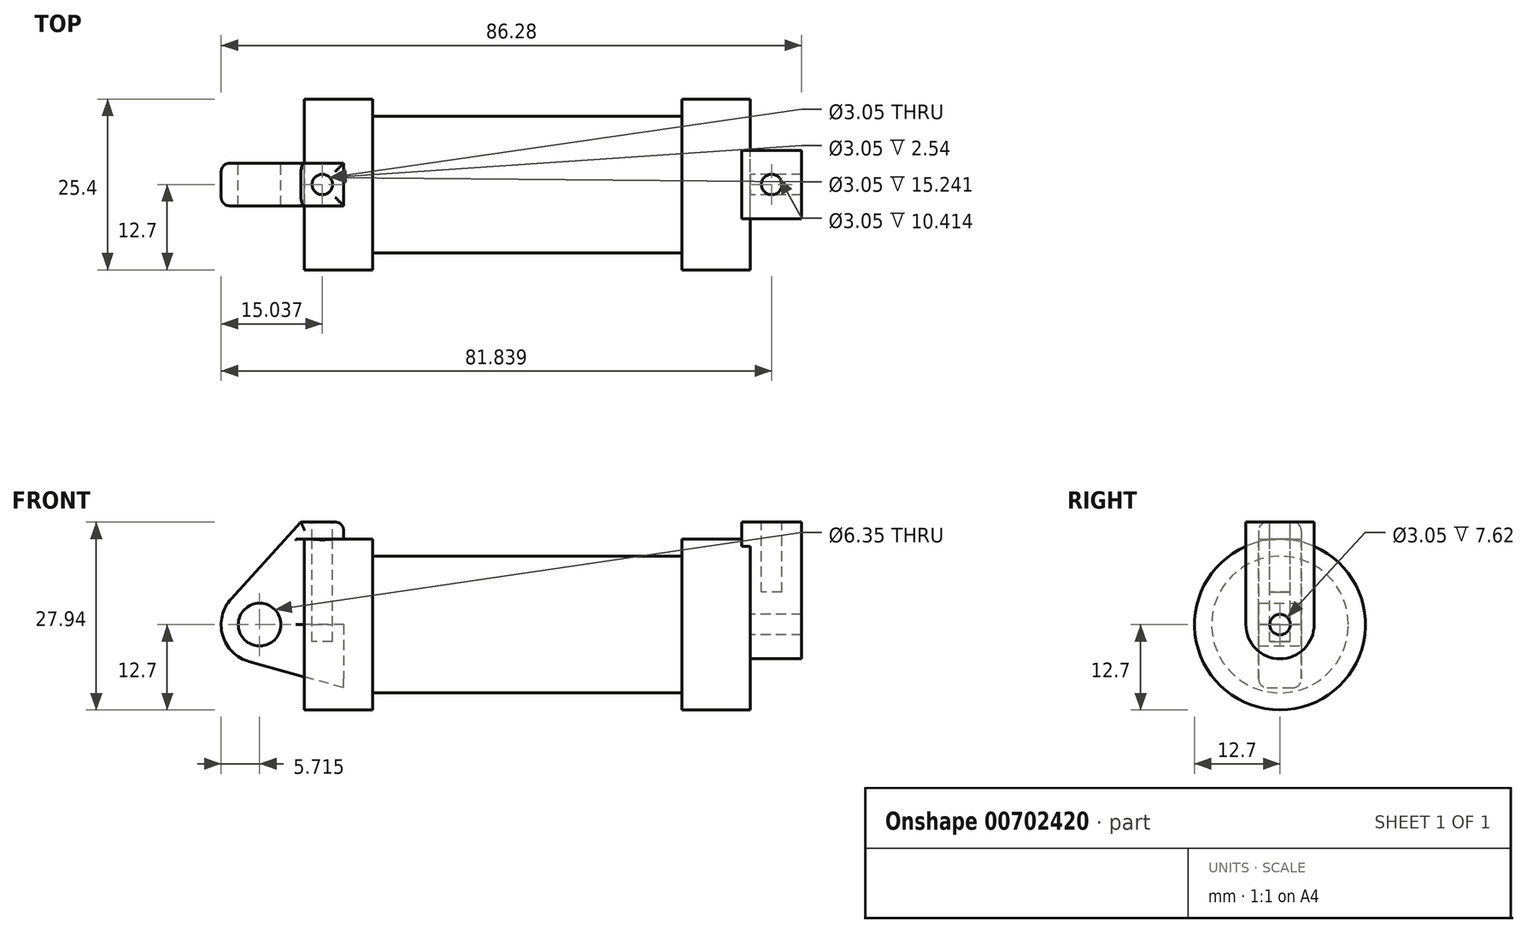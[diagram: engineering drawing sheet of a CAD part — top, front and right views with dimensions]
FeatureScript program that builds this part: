
annotation { "Feature Type Name" : "Feature", "Feature Type Description" : "" }
export const myFeature = defineFeature(function(context is Context, id is Id, definition is map)
    precondition{}
    {
        {
            var Q0;
            Q0=qCreatedBy(makeId("Front.planeOp"),FACE);
            var sketch = newSketch(context, id + "F0", { "sketchPlane" : qUnion([Q0])});
            skLineSegment(sketch, "E0", {"start": v(0, 0) * mm, "end": v(0, 12.7) * mm});
            skLineSegment(sketch, "E1", {"start": v(0, 12.7) * mm, "end": v(10.16, 12.7) * mm});
            skLineSegment(sketch, "E2", {"start": v(10.16, 12.7) * mm, "end": v(10.16, 10.16) * mm});
            skLineSegment(sketch, "E3", {"start": v(10.16, 10.16) * mm, "end": v(56.13, 10.16) * mm});
            skLineSegment(sketch, "E4", {"start": v(56.13, 10.16) * mm, "end": v(56.13, 12.7) * mm});
            skLineSegment(sketch, "E5", {"start": v(56.13, 12.7) * mm, "end": v(66.3, 12.7) * mm});
            skLineSegment(sketch, "E6", {"start": v(66.3, 12.7) * mm, "end": v(66.3, 0) * mm});
            skLineSegment(sketch, "E7", {"start": v(66.3, 0) * mm, "end": v(0, 0) * mm});
            skLineSegment(sketch, "E8", {"start": v(5.84, 15.24) * mm, "end": v(-0.5, 15.24) * mm});
            skLineSegment(sketch, "E9", {"start": v(-0.5, 15.24) * mm, "end": v(-10.88, 3.85) * mm});
            skLineSegment(sketch, "E10", {"start": v(0, 0) * mm, "end": v(-6.65, 0) * mm});
            skCircle(sketch, "E11", {"center": v(-6.65, 0) * mm, "radius": 5.72 * mm});
            skCircle(sketch, "E12", {"center": v(-6.65, 0) * mm, "radius": 3.18 * mm});
            skLineSegment(sketch, "E13", {"start": v(5.84, 15.24) * mm, "end": v(5.84, -9.4) * mm});
            skLineSegment(sketch, "E14", {"start": v(5.84, -9.4) * mm, "end": v(-8.18, -5.5) * mm});
            skSolve(sketch);
        }
        {
            var Q0;
            {var subQ0=sQuery(id+"F0.wireOp",EDGE,"E2");Q0=makeQuery(id+"F0.imprint","IMPRINT",FACE,{"disambiguationData":[TD([[makeQuery(id+"F0.imprint","IMPRINT",EDGE,{"derivedFrom":subQ0}),-1.0]])]});}
            var Q1;
            {var subQ0=sQuery(id+"F0.wireOp",EDGE,"E0");Q1=makeQuery(id+"F0.imprint","IMPRINT",FACE,{"disambiguationData":[TD([[makeQuery(id+"F0.imprint","IMPRINT",EDGE,{"derivedFrom":subQ0}),-1.0]])]});}
            var Q2;
            Q2=sQuery(id+"F0.wireOp",EDGE,"E3");
            var Q3;
            Q3=sQuery(id+"F0.wireOp",EDGE,"E7");
            revolve(context, id + "F1", {"entities" : qUnion([Q0, Q1]), "surfaceEntities" : qUnion([Q2]), "axis" : qUnion([Q3]), "revolveType" : RevolveType.FULL});
        }
        {
            var Q0;
            {var subQ1=sQuery(id+"F0.wireOp",EDGE,"E0");Q0=makeQuery(id+"F0.imprint","IMPRINT",FACE,{"disambiguationData":[TD([[makeQuery(id+"F0.imprint","IMPRINT",EDGE,{"derivedFrom":subQ1}),1.0]])]});}
            var Q1;
            {var subQ5=sQuery(id+"F0.wireOp",EDGE,"E12");Q1=makeQuery(id+"F0.imprint","IMPRINT",FACE,{"disambiguationData":[TD([[makeQuery(id+"F0.imprint","IMPRINT",EDGE,{"derivedFrom":subQ5}),-1.0]])]});}
            var Q2;
            {var subQ0=sQuery(id+"F0.wireOp",EDGE,"E14");Q2=makeQuery(id+"F0.imprint","IMPRINT",FACE,{"disambiguationData":[TD([[makeQuery(id+"F0.imprint","IMPRINT",EDGE,{"derivedFrom":subQ0}),-1.0]])]});}
            extrude(context, id + "F2", {"entities" : qUnion([Q0, Q1, Q2]), "endBound" : BoundingType.SYMMETRIC, "depth" : 6.35 * mm, "offsetDistance" : 25.4 * mm});
        }
        {
            var Q0;
            Q0=makeQuery(id+"F1.opRevolve","SWEPT_FACE",FACE,{"disambiguationData":[OSD([sQuery(id+"F0.wireOp",EDGE,"E6")])]});
            var sketch = newSketch(context, id + "F3", { "sketchPlane" : qUnion([Q0])});
            skCircle(sketch, "E15", {"center": v(0, 0) * mm, "radius": 1.52 * mm});
            skCircle(sketch, "E16", {"center": v(0, 0) * mm, "radius": 5.08 * mm});
            skLineSegment(sketch, "E17", {"start": v(5.08, 0) * mm, "end": v(5.08, 15.24) * mm});
            skLineSegment(sketch, "E18", {"start": v(-5.08, 0) * mm, "end": v(-5.08, 15.24) * mm});
            skLineSegment(sketch, "E19", {"start": v(-5.08, 15.24) * mm, "end": v(0, 15.24) * mm});
            skLineSegment(sketch, "E20", {"start": v(5.08, 15.24) * mm, "end": v(0, 15.24) * mm});
            skSolve(sketch);
        }
        {
            var Q0;
            {var subQ1=sQuery(id+"F3.wireOp",EDGE,"E19");Q0=makeQuery(id+"F3.imprint","IMPRINT",FACE,{"disambiguationData":[TD([[makeQuery(id+"F3.imprint","IMPRINT",EDGE,{"derivedFrom":subQ1}),-1.0]])]});}
            var Q1;
            {var subQ0=sQuery(id+"F3.wireOp",EDGE,"E17");var subQ1=sQuery(id+"F3.wireOp",EDGE,"E16");var subQ2=makeQuery(id+"F3.imprint","INTERSECT",VERTEX,{"derivedFrom":[subQ1,subQ0]});Q1=makeQuery(id+"F3.imprint","IMPRINT",FACE,{"disambiguationData":[TD([[makeQuery(id+"F3.imprint","IMPRINT",EDGE,{"disambiguationData":[TD([[subQ2,-1.0]])],"derivedFrom":subQ1}),-1.0]])]});}
            var Q2;
            Q2=makeQuery(id+"F3.imprint","IMPRINT",FACE,{"disambiguationData":[TD([[makeQuery(id+"F3.imprint","IMPRINT",EDGE,{"derivedFrom":sQuery(id+"F3.wireOp",EDGE,"E15")}),-1.0]])]});
            extrude(context, id + "F4", {"entities" : qUnion([Q0, Q1, Q2]), "operationType" : NewBodyOperationType.ADD, "oppositeDirection" : true, "depth" : 1.27 * mm, "offsetDistance" : 25.4 * mm});
        }
        {
            var Q0;
            {var subQ1=sQuery(id+"F3.wireOp",EDGE,"E19");Q0=makeQuery(id+"F3.imprint","IMPRINT",FACE,{"disambiguationData":[TD([[makeQuery(id+"F3.imprint","IMPRINT",EDGE,{"derivedFrom":subQ1}),-1.0]])]});}
            var Q1;
            {var subQ0=sQuery(id+"F3.wireOp",EDGE,"E17");var subQ1=sQuery(id+"F3.wireOp",EDGE,"E16");var subQ2=makeQuery(id+"F3.imprint","INTERSECT",VERTEX,{"derivedFrom":[subQ1,subQ0]});Q1=makeQuery(id+"F3.imprint","IMPRINT",FACE,{"disambiguationData":[TD([[makeQuery(id+"F3.imprint","IMPRINT",EDGE,{"disambiguationData":[TD([[subQ2,-1.0]])],"derivedFrom":subQ1}),-1.0]])]});}
            var Q2;
            Q2=makeQuery(id+"F3.imprint","IMPRINT",FACE,{"disambiguationData":[TD([[makeQuery(id+"F3.imprint","IMPRINT",EDGE,{"derivedFrom":sQuery(id+"F3.wireOp",EDGE,"E15")}),-1.0]])]});
            extrude(context, id + "F5", {"entities" : qUnion([Q0, Q1, Q2]), "operationType" : NewBodyOperationType.ADD, "depth" : 7.62 * mm, "offsetDistance" : 25.4 * mm});
        }
        {
            var Q0;
            Q0=makeQuery(id+"F2.opExtrude","SWEPT_FACE",FACE,{"disambiguationData":[OSD([sQuery(id+"F0.wireOp",EDGE,"E8")])]});
            var sketch = newSketch(context, id + "F6", { "sketchPlane" : qUnion([Q0])});
            skCircle(sketch, "E21", {"center": v(2.67, 0) * mm, "radius": 1.52 * mm});
            skPoint(sketch, "E21.centerSnap0", {"position": v(2.67, 3.18) * mm});
            skPoint(sketch, "E21.centerSnap1", {"position": v(5.84, 0) * mm});
            skSolve(sketch);
        }
        {
            var Q0;
            {var subQ0=sQuery(id+"F3.wireOp",EDGE,"E20");var subQ1=sQuery(id+"F3.wireOp",EDGE,"E19");Q0=makeQuery(id+"F5.boolean.opBoolean","MERGE",FACE,{"derivedFrom":[makeQuery(id+"F4.opExtrude","SWEPT_FACE",FACE,{"disambiguationData":[OSD([subQ1,subQ0])]}),makeQuery(id+"F5.opExtrude","SWEPT_FACE",FACE,{"disambiguationData":[OSD([subQ1,subQ0])]})]});}
            var sketch = newSketch(context, id + "F7", { "sketchPlane" : qUnion([Q0])});
            skCircle(sketch, "E22", {"center": v(69.47, 0) * mm, "radius": 1.52 * mm});
            skPoint(sketch, "E22.centerSnap0", {"position": v(65.02, 0) * mm});
            skPoint(sketch, "E22.centerSnap1", {"position": v(69.47, -5.08) * mm});
            skSolve(sketch);
        }
        {
            var Q0;
            Q0=makeQuery(id+"F6.imprint","IMPRINT",FACE,{"disambiguationData":[TD([[makeQuery(id+"F6.imprint","IMPRINT",EDGE,{"derivedFrom":sQuery(id+"F6.wireOp",EDGE,"E21")}),1.0]])]});
            extrude(context, id + "F8", {"entities" : qUnion([Q0]), "operationType" : NewBodyOperationType.REMOVE, "oppositeDirection" : true, "depth" : 17.78 * mm, "offsetDistance" : 25.4 * mm});
        }
        {
            var Q0;
            Q0=makeQuery(id+"F7.imprint","IMPRINT",FACE,{"disambiguationData":[TD([[makeQuery(id+"F7.imprint","IMPRINT",EDGE,{"derivedFrom":sQuery(id+"F7.wireOp",EDGE,"E22")}),1.0]])]});
            extrude(context, id + "F9", {"entities" : qUnion([Q0]), "operationType" : NewBodyOperationType.REMOVE, "oppositeDirection" : true, "depth" : 10.4 * mm, "offsetDistance" : 25.4 * mm});
        }
        {
            var Q0;
            Q0=makeQuery(id+"F1.opRevolve","SWEPT_EDGE",EDGE,{"disambiguationData":[OSD([sQuery(id+"F0.wireOp",EDGE,"E1"),sQuery(id+"F0.wireOp",EDGE,"E2")])]});
            var Q1;
            Q1=makeQuery(id+"F2.opExtrude","SWEPT_EDGE",EDGE,{"disambiguationData":[OSD([sQuery(id+"F0.wireOp",EDGE,"E8"),sQuery(id+"F0.wireOp",EDGE,"E13")])]});
            var Q2;
            Q2=makeQuery(id+"F2.opExtrude","CAP_EDGE",EDGE,{"disambiguationData":[OSD([sQuery(id+"F0.wireOp",EDGE,"E9")])],"isStart":false});
            var Q3;
            Q3=makeQuery(id+"F2.opExtrude","CAP_EDGE",EDGE,{"disambiguationData":[OSD([sQuery(id+"F0.wireOp",EDGE,"E8")])],"isStart":false});
            var Q4;
            Q4=makeQuery(id+"F2.opExtrude","CAP_EDGE",EDGE,{"disambiguationData":[OSD([sQuery(id+"F0.wireOp",EDGE,"E8")])],"isStart":true});
            var Q5;
            Q5=makeQuery(id+"F2.opExtrude","CAP_EDGE",EDGE,{"disambiguationData":[OSD([sQuery(id+"F0.wireOp",EDGE,"E9")])],"isStart":true});
            var Q6;
            Q6=makeQuery(id+"F1.opRevolve","SWEPT_EDGE",EDGE,{"disambiguationData":[OSD([sQuery(id+"F0.wireOp",EDGE,"E0"),sQuery(id+"F0.wireOp",EDGE,"E1")])]});
            var Q7;
            Q7=makeQuery(id+"F1.opRevolve","SWEPT_EDGE",EDGE,{"disambiguationData":[OSD([sQuery(id+"F0.wireOp",EDGE,"E4"),sQuery(id+"F0.wireOp",EDGE,"E5")])]});
            var Q8;
            Q8=makeQuery(id+"F1.opRevolve","SWEPT_EDGE",EDGE,{"disambiguationData":[OSD([sQuery(id+"F0.wireOp",EDGE,"E5"),sQuery(id+"F0.wireOp",EDGE,"E6")])]});
            var Q9;
            {var subQ0=sQuery(id+"F3.wireOp",EDGE,"E20");var subQ1=sQuery(id+"F3.wireOp",EDGE,"E17");Q9=makeQuery(id+"F5.boolean.opBoolean","MERGE",EDGE,{"derivedFrom":[makeQuery(id+"F4.opExtrude","SWEPT_EDGE",EDGE,{"disambiguationData":[OSD([subQ1,subQ0])]}),makeQuery(id+"F5.opExtrude","SWEPT_EDGE",EDGE,{"disambiguationData":[OSD([subQ1,subQ0])]})]});}
            var Q10;
            Q10=makeQuery(id+"F5.opExtrude","CAP_EDGE",EDGE,{"disambiguationData":[OSD([sQuery(id+"F3.wireOp",EDGE,"E17")])],"isStart":false});
            var Q11;
            {var subQ0=sQuery(id+"F3.wireOp",EDGE,"E19");var subQ1=sQuery(id+"F3.wireOp",EDGE,"E18");Q11=makeQuery(id+"F5.boolean.opBoolean","MERGE",EDGE,{"derivedFrom":[makeQuery(id+"F4.opExtrude","SWEPT_EDGE",EDGE,{"disambiguationData":[OSD([subQ1,subQ0])]}),makeQuery(id+"F5.opExtrude","SWEPT_EDGE",EDGE,{"disambiguationData":[OSD([subQ1,subQ0])]})]});}
            var Q12;
            Q12=makeQuery(id+"F5.opExtrude","CAP_EDGE",EDGE,{"disambiguationData":[OSD([sQuery(id+"F3.wireOp",EDGE,"E19"),sQuery(id+"F3.wireOp",EDGE,"E20")])],"isStart":false});
            var Q13;
            Q13=makeQuery(id+"F4.opExtrude","CAP_EDGE",EDGE,{"disambiguationData":[OSD([sQuery(id+"F3.wireOp",EDGE,"E19"),sQuery(id+"F3.wireOp",EDGE,"E20")])],"isStart":false});
            var Q14;
            Q14=makeQuery(id+"F5.opExtrude","CAP_EDGE",EDGE,{"disambiguationData":[OSD([sQuery(id+"F3.wireOp",EDGE,"E18")])],"isStart":true});
            var Q15;
            Q15=makeQuery(id+"F2.opExtrude","CAP_EDGE",EDGE,{"disambiguationData":[OSD([sQuery(id+"F0.wireOp",EDGE,"E0")])],"isStart":false});
            var Q16;
            Q16=makeQuery(id+"F2.opExtrude","CAP_EDGE",EDGE,{"disambiguationData":[OSD([sQuery(id+"F0.wireOp",EDGE,"E0")])],"isStart":true});
            fillet(context, id + "F10", {"entities" : qUnion([Q0, Q1, Q2, Q3, Q4, Q5, Q6, Q7, Q8, Q9, Q10, Q11, Q12, Q13, Q14, Q15, Q16]), "radius" : 1.27 * mm, "tangentPropagation" : true, "allowEdgeOverflow" : false});
        }
    });
